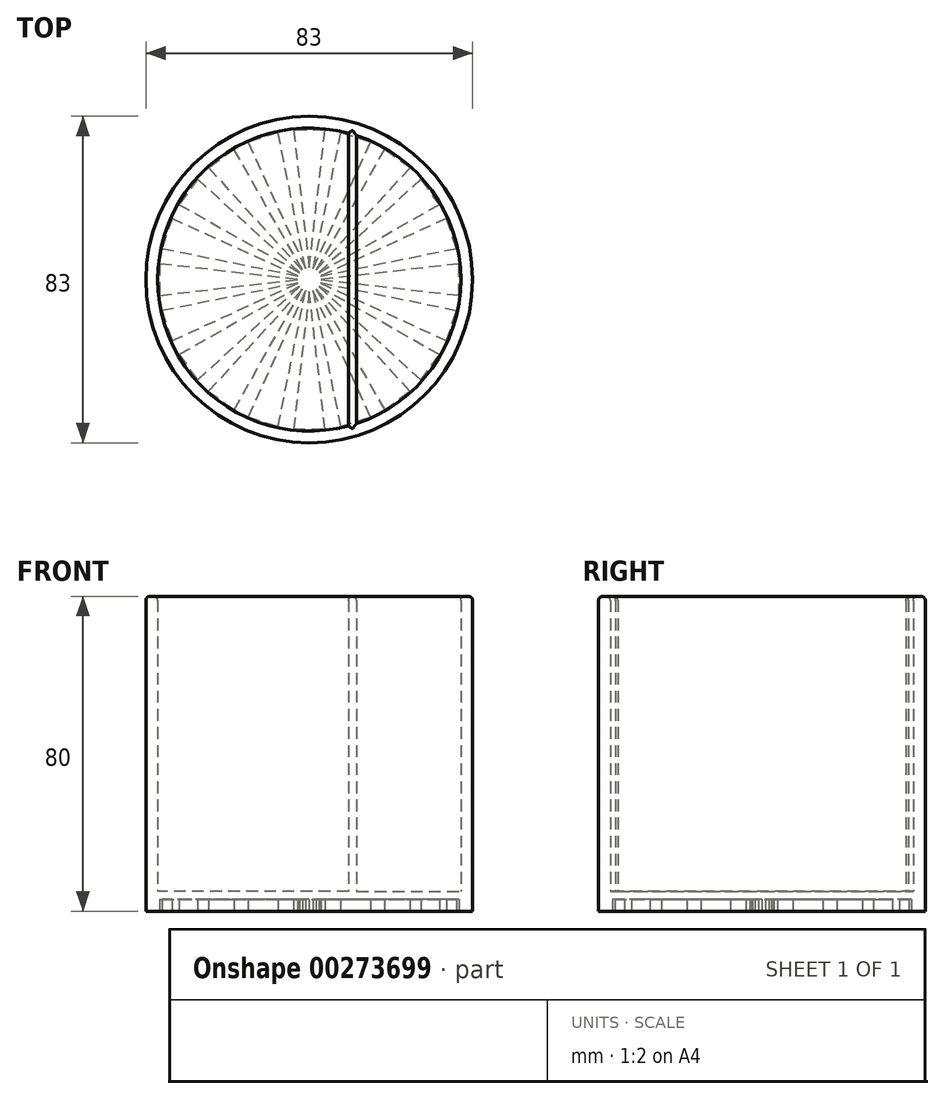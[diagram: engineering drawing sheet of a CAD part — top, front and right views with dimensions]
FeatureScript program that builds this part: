
annotation { "Feature Type Name" : "Feature", "Feature Type Description" : "" }
export const myFeature = defineFeature(function(context is Context, id is Id, definition is map)
    precondition{}
    {
        {
            var Q0;
            Q0=qCreatedBy(makeId("Top.planeOp"),FACE);
            var sketch = newSketch(context, id + "F0", { "sketchPlane" : qUnion([Q0])});
            skCircle(sketch, "E0", {"center": v(0, 0) * mm, "radius": 41.5 * mm});
            skCircle(sketch, "E1", {"center": v(0, 0) * mm, "radius": 38.5 * mm});
            skSolve(sketch);
        }
        {
            var Q0;
            Q0=qCreatedBy(makeId("Top.planeOp"),FACE);
            var sketch = newSketch(context, id + "F1", { "sketchPlane" : qUnion([Q0])});
            skLineSegment(sketch, "E2.bottom", {"start": v(10, 37.18) * mm, "end": v(12, 37.18) * mm});
            skLineSegment(sketch, "E2.top", {"start": v(10, -37.18) * mm, "end": v(12, -37.18) * mm});
            skLineSegment(sketch, "E2.left", {"start": v(10, 37.18) * mm, "end": v(10, -37.18) * mm});
            skLineSegment(sketch, "E2.right", {"start": v(12, 37.18) * mm, "end": v(12, -37.18) * mm});
            skSolve(sketch);
        }
        {
            var Q0;
            Q0=makeQuery(id+"F0.imprint","IMPRINT",FACE,{"disambiguationData":[TD([[makeQuery(id+"F0.imprint","IMPRINT",EDGE,{"derivedFrom":sQuery(id+"F0.wireOp",EDGE,"E1")}),1.0]])]});
            extrude(context, id + "F2", {"entities" : qUnion([Q0]), "depth" : 5 * mm});
        }
        {
            var Q0;
            Q0=makeQuery(id+"F0.imprint","IMPRINT",FACE,{"disambiguationData":[TD([[makeQuery(id+"F0.imprint","IMPRINT",EDGE,{"derivedFrom":sQuery(id+"F0.wireOp",EDGE,"E0")}),1.0]])]});
            var Q1;
            Q1=makeQuery(id+"F1.imprint","IMPRINT",FACE,{"disambiguationData":[TD([[makeQuery(id+"F1.imprint","IMPRINT",EDGE,{"derivedFrom":sQuery(id+"F1.wireOp",EDGE,"E2.bottom")}),-1.0]])]});
            extrude(context, id + "F3", {"entities" : qUnion([Q0, Q1]), "operationType" : NewBodyOperationType.ADD, "depth" : 80 * mm});
        }
        {
            var Q0;
            Q0=qCreatedBy(makeId("Top.planeOp"),FACE);
            var sketch = newSketch(context, id + "F4", { "sketchPlane" : qUnion([Q0])});
            skLineSegment(sketch, "E3", {"start": v(-4, -38) * mm, "end": v(4, -38) * mm});
            skLineSegment(sketch, "E4", {"start": v(4, -38) * mm, "end": v(0, -3) * mm});
            skLineSegment(sketch, "E5", {"start": v(0, -3) * mm, "end": v(-4, -38) * mm});
            skLineSegment(sketch, "E6.1.0", {"start": v(0.93, -2.85) * mm, "end": v(7.94, -37.38) * mm});
            skLineSegment(sketch, "E6.1.1", {"start": v(15.55, -34.9) * mm, "end": v(0.93, -2.85) * mm});
            skLineSegment(sketch, "E6.1.2", {"start": v(7.94, -37.38) * mm, "end": v(15.55, -34.9) * mm});
            skLineSegment(sketch, "E6.2.0", {"start": v(1.76, -2.43) * mm, "end": v(19.1, -33.1) * mm});
            skLineSegment(sketch, "E6.2.1", {"start": v(25.57, -28.4) * mm, "end": v(1.76, -2.43) * mm});
            skLineSegment(sketch, "E6.2.2", {"start": v(19.1, -33.1) * mm, "end": v(25.57, -28.4) * mm});
            skLineSegment(sketch, "E6.3.0", {"start": v(2.43, -1.76) * mm, "end": v(28.4, -25.57) * mm});
            skLineSegment(sketch, "E6.3.1", {"start": v(33.1, -19.1) * mm, "end": v(2.43, -1.76) * mm});
            skLineSegment(sketch, "E6.3.2", {"start": v(28.4, -25.57) * mm, "end": v(33.1, -19.1) * mm});
            skLineSegment(sketch, "E6.4.0", {"start": v(2.85, -0.93) * mm, "end": v(34.9, -15.55) * mm});
            skLineSegment(sketch, "E6.4.1", {"start": v(37.38, -7.94) * mm, "end": v(2.85, -0.93) * mm});
            skLineSegment(sketch, "E6.4.2", {"start": v(34.9, -15.55) * mm, "end": v(37.38, -7.94) * mm});
            skLineSegment(sketch, "E6.5.0", {"start": v(3, 0) * mm, "end": v(38, -4) * mm});
            skLineSegment(sketch, "E6.5.1", {"start": v(38, 4) * mm, "end": v(3, 0) * mm});
            skLineSegment(sketch, "E6.5.2", {"start": v(38, -4) * mm, "end": v(38, 4) * mm});
            skLineSegment(sketch, "E6.6.0", {"start": v(2.85, 0.93) * mm, "end": v(37.38, 7.94) * mm});
            skLineSegment(sketch, "E6.6.1", {"start": v(34.9, 15.55) * mm, "end": v(2.85, 0.93) * mm});
            skLineSegment(sketch, "E6.6.2", {"start": v(37.38, 7.94) * mm, "end": v(34.9, 15.55) * mm});
            skLineSegment(sketch, "E6.7.0", {"start": v(2.43, 1.76) * mm, "end": v(33.1, 19.1) * mm});
            skLineSegment(sketch, "E6.7.1", {"start": v(28.4, 25.57) * mm, "end": v(2.43, 1.76) * mm});
            skLineSegment(sketch, "E6.7.2", {"start": v(33.1, 19.1) * mm, "end": v(28.4, 25.57) * mm});
            skLineSegment(sketch, "E6.8.0", {"start": v(1.76, 2.43) * mm, "end": v(25.57, 28.4) * mm});
            skLineSegment(sketch, "E6.8.1", {"start": v(19.1, 33.1) * mm, "end": v(1.76, 2.43) * mm});
            skLineSegment(sketch, "E6.8.2", {"start": v(25.57, 28.4) * mm, "end": v(19.1, 33.1) * mm});
            skLineSegment(sketch, "E6.9.0", {"start": v(0.93, 2.85) * mm, "end": v(15.55, 34.9) * mm});
            skLineSegment(sketch, "E6.9.1", {"start": v(7.94, 37.38) * mm, "end": v(0.93, 2.85) * mm});
            skLineSegment(sketch, "E6.9.2", {"start": v(15.55, 34.9) * mm, "end": v(7.94, 37.38) * mm});
            skLineSegment(sketch, "E6.10.0", {"start": v(0, 3) * mm, "end": v(4, 38) * mm});
            skLineSegment(sketch, "E6.10.1", {"start": v(-4, 38) * mm, "end": v(0, 3) * mm});
            skLineSegment(sketch, "E6.10.2", {"start": v(4, 38) * mm, "end": v(-4, 38) * mm});
            skLineSegment(sketch, "E6.11.0", {"start": v(-0.93, 2.85) * mm, "end": v(-7.94, 37.38) * mm});
            skLineSegment(sketch, "E6.11.1", {"start": v(-15.55, 34.9) * mm, "end": v(-0.93, 2.85) * mm});
            skLineSegment(sketch, "E6.11.2", {"start": v(-7.94, 37.38) * mm, "end": v(-15.55, 34.9) * mm});
            skLineSegment(sketch, "E6.12.0", {"start": v(-1.76, 2.43) * mm, "end": v(-19.1, 33.1) * mm});
            skLineSegment(sketch, "E6.12.1", {"start": v(-25.57, 28.4) * mm, "end": v(-1.76, 2.43) * mm});
            skLineSegment(sketch, "E6.12.2", {"start": v(-19.1, 33.1) * mm, "end": v(-25.57, 28.4) * mm});
            skLineSegment(sketch, "E6.13.0", {"start": v(-2.43, 1.76) * mm, "end": v(-28.4, 25.57) * mm});
            skLineSegment(sketch, "E6.13.1", {"start": v(-33.1, 19.1) * mm, "end": v(-2.43, 1.76) * mm});
            skLineSegment(sketch, "E6.13.2", {"start": v(-28.4, 25.57) * mm, "end": v(-33.1, 19.1) * mm});
            skLineSegment(sketch, "E6.14.0", {"start": v(-2.85, 0.93) * mm, "end": v(-34.9, 15.55) * mm});
            skLineSegment(sketch, "E6.14.1", {"start": v(-37.38, 7.94) * mm, "end": v(-2.85, 0.93) * mm});
            skLineSegment(sketch, "E6.14.2", {"start": v(-34.9, 15.55) * mm, "end": v(-37.38, 7.94) * mm});
            skLineSegment(sketch, "E6.15.0", {"start": v(-3, 0) * mm, "end": v(-38, 4) * mm});
            skLineSegment(sketch, "E6.15.1", {"start": v(-38, -4) * mm, "end": v(-3, 0) * mm});
            skLineSegment(sketch, "E6.15.2", {"start": v(-38, 4) * mm, "end": v(-38, -4) * mm});
            skLineSegment(sketch, "E6.16.0", {"start": v(-2.85, -0.93) * mm, "end": v(-37.38, -7.94) * mm});
            skLineSegment(sketch, "E6.16.1", {"start": v(-34.9, -15.55) * mm, "end": v(-2.85, -0.93) * mm});
            skLineSegment(sketch, "E6.16.2", {"start": v(-37.38, -7.94) * mm, "end": v(-34.9, -15.55) * mm});
            skLineSegment(sketch, "E6.17.0", {"start": v(-2.43, -1.76) * mm, "end": v(-33.1, -19.1) * mm});
            skLineSegment(sketch, "E6.17.1", {"start": v(-28.4, -25.57) * mm, "end": v(-2.43, -1.76) * mm});
            skLineSegment(sketch, "E6.17.2", {"start": v(-33.1, -19.1) * mm, "end": v(-28.4, -25.57) * mm});
            skLineSegment(sketch, "E6.18.0", {"start": v(-1.76, -2.43) * mm, "end": v(-25.57, -28.4) * mm});
            skLineSegment(sketch, "E6.18.1", {"start": v(-19.1, -33.1) * mm, "end": v(-1.76, -2.43) * mm});
            skLineSegment(sketch, "E6.18.2", {"start": v(-25.57, -28.4) * mm, "end": v(-19.1, -33.1) * mm});
            skLineSegment(sketch, "E6.19.0", {"start": v(-0.93, -2.85) * mm, "end": v(-15.55, -34.9) * mm});
            skLineSegment(sketch, "E6.19.1", {"start": v(-7.94, -37.38) * mm, "end": v(-0.93, -2.85) * mm});
            skLineSegment(sketch, "E6.19.2", {"start": v(-15.55, -34.9) * mm, "end": v(-7.94, -37.38) * mm});
            skPoint(sketch, "E6.center", {"position": v(0, 0) * mm});
            skSolve(sketch);
        }
        {
            var Q0;
            Q0 = qSketchRegion(id + "F4", true);
            extrude(context, id + "F5", {"entities" : qUnion([Q0]), "operationType" : NewBodyOperationType.REMOVE, "depth" : 3 * mm});
        }
        {
            var Q0;
            {var subQ0=sQuery(id+"F0.wireOp",EDGE,"E1");var subQ1=sQuery(id+"F1.wireOp",EDGE,"E2.right");Q0=makeQuery(id+"F3.boolean.opBoolean","SPLIT",EDGE,{"disambiguationData":[TD([makeQuery(id+"F3.opExtrude","SWEPT_FACE",FACE,{"disambiguationData":[OSD([subQ1])]})])],"derivedFrom":makeQuery(id+"F3.opExtrude","CAP_EDGE",EDGE,{"disambiguationData":[OSD([subQ0])],"isStart":false})});}
            var Q1;
            Q1=makeQuery(id+"F3.opExtrude","CAP_EDGE",EDGE,{"disambiguationData":[OSD([sQuery(id+"F0.wireOp",EDGE,"E0")])],"isStart":false});
            var Q2;
            {var subQ0=sQuery(id+"F0.wireOp",EDGE,"E1");var subQ1=sQuery(id+"F1.wireOp",EDGE,"E2.left");Q2=makeQuery(id+"F3.boolean.opBoolean","SPLIT",EDGE,{"disambiguationData":[TD([makeQuery(id+"F3.opExtrude","SWEPT_FACE",FACE,{"disambiguationData":[OSD([subQ1])]})])],"derivedFrom":makeQuery(id+"F3.opExtrude","CAP_EDGE",EDGE,{"disambiguationData":[OSD([subQ0])],"isStart":false})});}
            var Q3;
            Q3=makeQuery(id+"F3.opExtrude","CAP_EDGE",EDGE,{"disambiguationData":[OSD([sQuery(id+"F1.wireOp",EDGE,"E2.right")])],"isStart":false});
            var Q4;
            Q4=makeQuery(id+"F3.opExtrude","CAP_EDGE",EDGE,{"disambiguationData":[OSD([sQuery(id+"F1.wireOp",EDGE,"E2.left")])],"isStart":false});
            fillet(context, id + "F6", {"entities" : qUnion([Q0, Q1, Q2, Q3, Q4]), "radius" : 1 * mm, "tangentPropagation" : true, "allowEdgeOverflow" : false});
        }
    });
